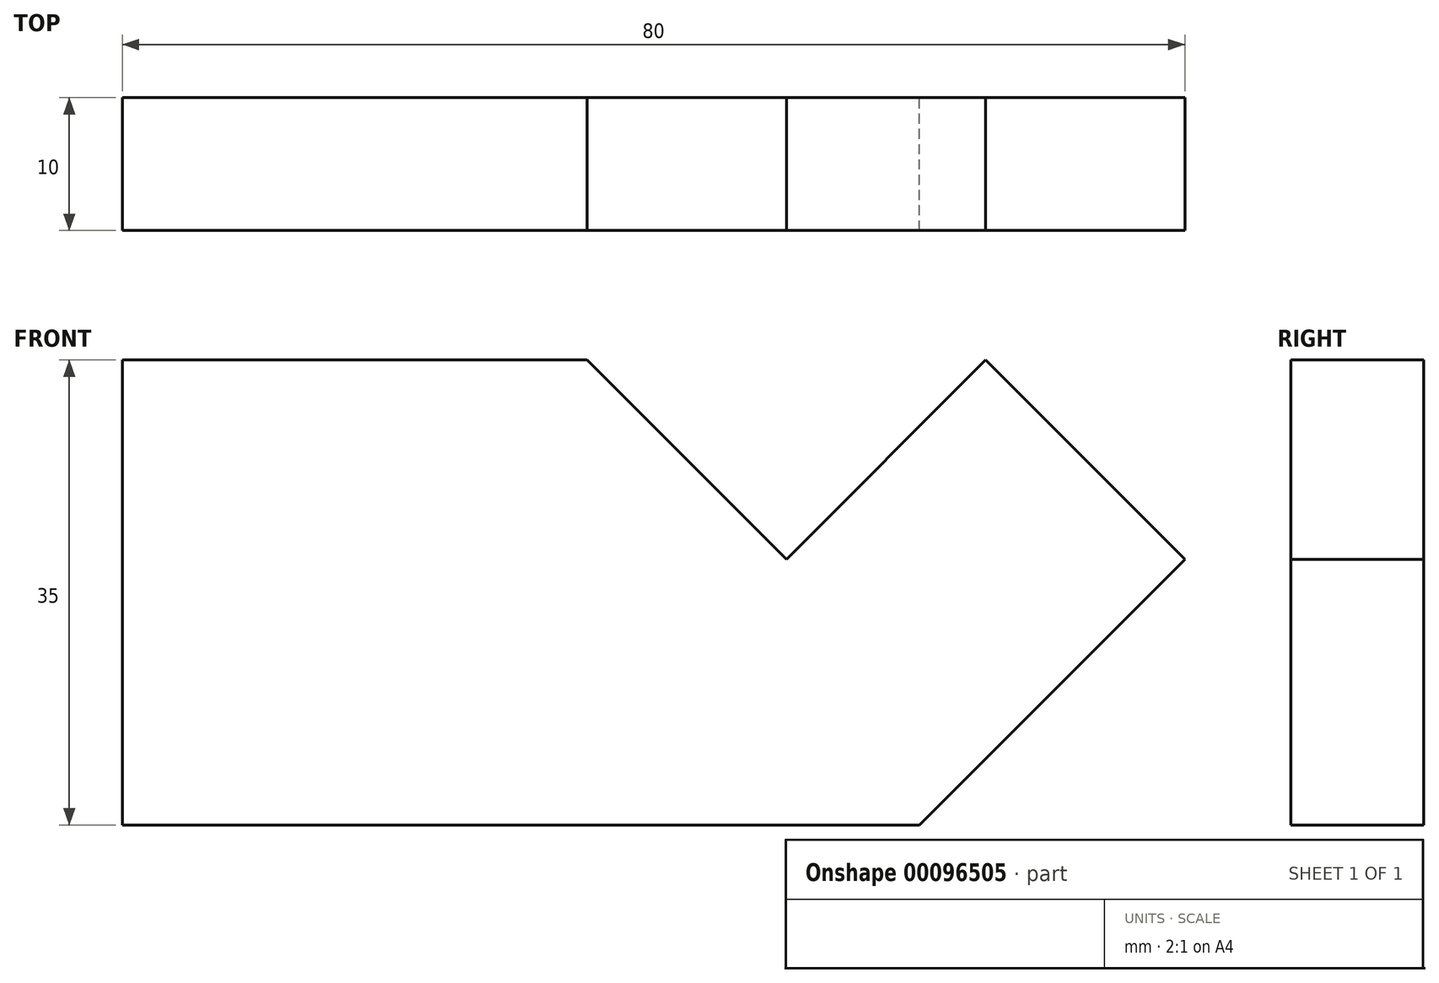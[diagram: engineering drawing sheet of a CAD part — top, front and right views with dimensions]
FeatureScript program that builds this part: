
annotation { "Feature Type Name" : "Feature", "Feature Type Description" : "" }
export const myFeature = defineFeature(function(context is Context, id is Id, definition is map)
    precondition{}
    {
        {
            var Q0;
            Q0=qCreatedBy(makeId("Front.planeOp"),FACE);
            var sketch = newSketch(context, id + "F0", { "sketchPlane" : qUnion([Q0])});
            skLineSegment(sketch, "E0", {"start": v(0, 0) * mm, "end": v(60, 0) * mm});
            skLineSegment(sketch, "E1", {"start": v(60, 0) * mm, "end": v(80, 20) * mm});
            skLineSegment(sketch, "E2", {"start": v(80, 20) * mm, "end": v(65, 35) * mm});
            skLineSegment(sketch, "E3", {"start": v(65, 35) * mm, "end": v(50, 20) * mm});
            skLineSegment(sketch, "E4", {"start": v(50, 20) * mm, "end": v(35, 35) * mm});
            skLineSegment(sketch, "E5", {"start": v(35, 35) * mm, "end": v(0, 35) * mm});
            skLineSegment(sketch, "E6", {"start": v(0, 35) * mm, "end": v(0, 0) * mm});
            skSolve(sketch);
        }
        {
            var Q0;
            Q0 = qSketchRegion(id + "F0", true);
            extrude(context, id + "F1", {"entities" : qUnion([Q0]), "depth" : 10 * mm});
        }
    });
